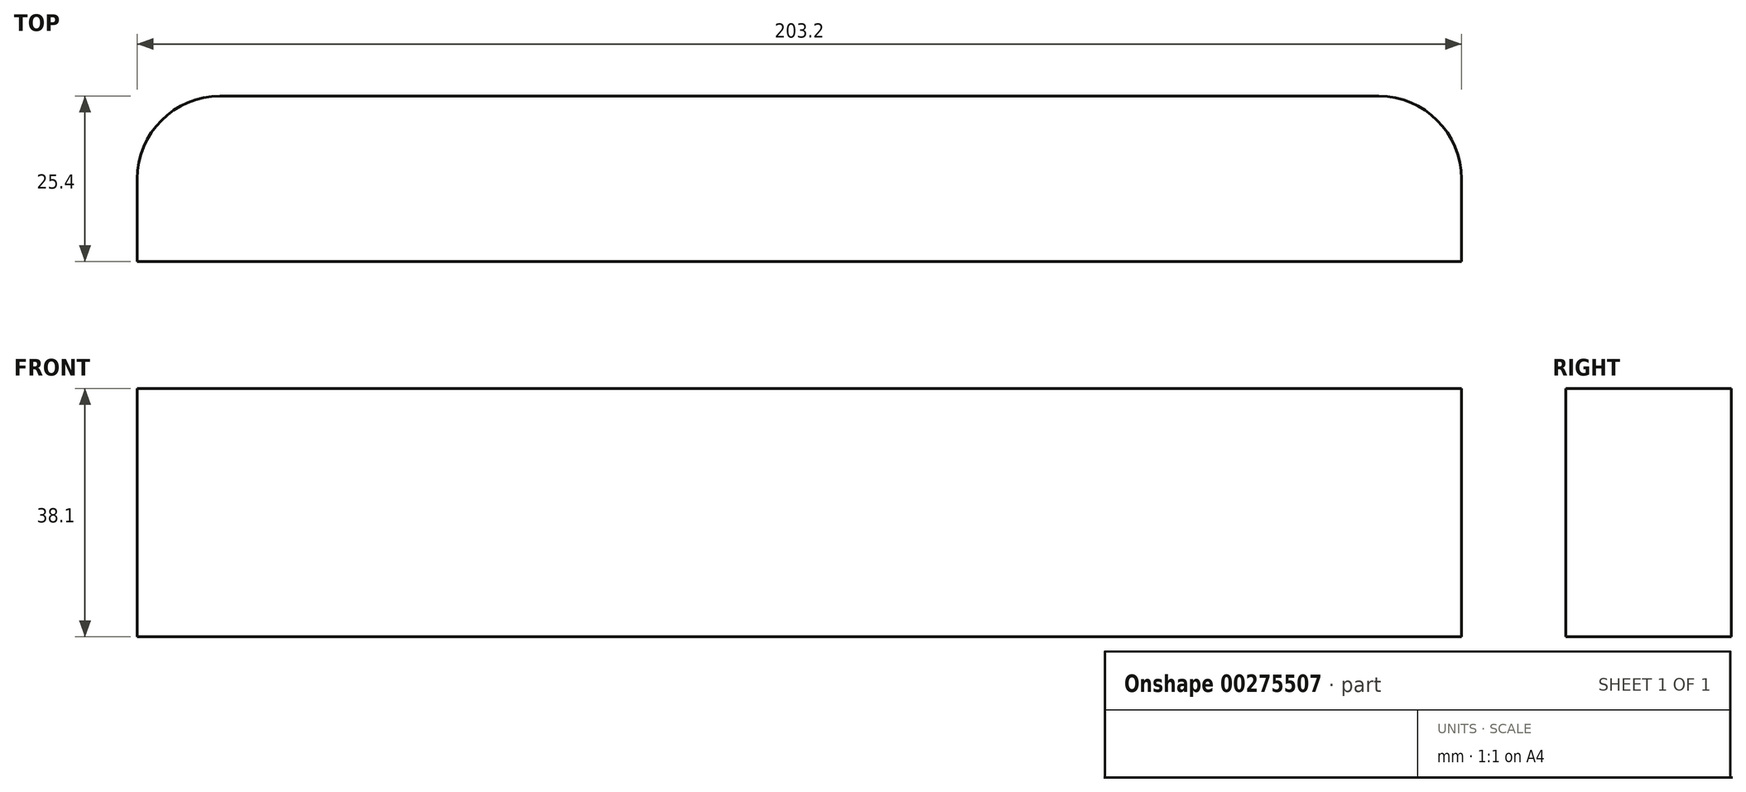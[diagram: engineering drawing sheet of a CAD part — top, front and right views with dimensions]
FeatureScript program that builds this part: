
annotation { "Feature Type Name" : "Feature", "Feature Type Description" : "" }
export const myFeature = defineFeature(function(context is Context, id is Id, definition is map)
    precondition{}
    {
        {
            var Q0;
            Q0=qCreatedBy(makeId("Top.planeOp"),FACE);
            var sketch = newSketch(context, id + "F0", { "sketchPlane" : qUnion([Q0])});
            skLineSegment(sketch, "E0.bottom", {"start": v(-80.27, 58.74) * mm, "end": v(97.53, 58.74) * mm});
            skLineSegment(sketch, "E0.top", {"start": v(-92.97, 33.34) * mm, "end": v(110.23, 33.34) * mm});
            skLineSegment(sketch, "E0.left", {"start": v(-92.97, 46.04) * mm, "end": v(-92.97, 33.34) * mm});
            skLineSegment(sketch, "E0.right", {"start": v(110.23, 46.04) * mm, "end": v(110.23, 33.34) * mm});
            skLineSegment(sketch, "E1.bottom", {"start": v(-92.97, 33.34) * mm, "end": v(-57.4, 33.34) * mm});
            skLineSegment(sketch, "E1.top", {"start": v(-92.97, -42.86) * mm, "end": v(-57.4, -42.86) * mm});
            skLineSegment(sketch, "E1.left", {"start": v(-92.97, 33.34) * mm, "end": v(-92.97, -42.86) * mm});
            skLineSegment(sketch, "E1.right", {"start": v(-57.4, 33.34) * mm, "end": v(-57.4, -42.86) * mm});
            skLineSegment(sketch, "E2.bottom", {"start": v(110.23, 33.34) * mm, "end": v(74.67, 33.34) * mm});
            skLineSegment(sketch, "E2.top", {"start": v(110.23, -42.86) * mm, "end": v(74.67, -42.86) * mm});
            skLineSegment(sketch, "E2.left", {"start": v(110.23, 33.34) * mm, "end": v(110.23, -42.86) * mm});
            skLineSegment(sketch, "E2.right", {"start": v(74.67, 33.34) * mm, "end": v(74.67, -42.86) * mm});
            skPoint(sketch, "E3.visualSharp", {"position": v(-92.97, 58.74) * mm});
            skArc(sketch, "E3.filletArc", {"start": v(-80.27, 58.74) * mm, "mid": v(-89.25, 55.02) * mm, "end": v(-92.97, 46.04) * mm});
            skPoint(sketch, "E4.visualSharp", {"position": v(110.23, 58.74) * mm});
            skArc(sketch, "E4.filletArc", {"start": v(110.23, 46.04) * mm, "mid": v(106.51, 55.02) * mm, "end": v(97.53, 58.74) * mm});
            skSolve(sketch);
        }
        {
            var Q0;
            Q0=makeQuery(id+"F0.imprint","IMPRINT",FACE,{"disambiguationData":[TD([[makeQuery(id+"F0.imprint","IMPRINT",EDGE,{"derivedFrom":sQuery(id+"F0.wireOp",EDGE,"E0.bottom")}),-1.0]])]});
            var Q1;
            Q1=makeQuery(id+"F0.imprint","IMPRINT",FACE,{"disambiguationData":[TD([[makeQuery(id+"F0.imprint","IMPRINT",EDGE,{"derivedFrom":sQuery(id+"F0.wireOp",EDGE,"E1.bottom")}),-1.0]])]});
            var Q2;
            Q2=makeQuery(id+"F0.imprint","IMPRINT",FACE,{"disambiguationData":[TD([[makeQuery(id+"F0.imprint","IMPRINT",EDGE,{"derivedFrom":sQuery(id+"F0.wireOp",EDGE,"E2.bottom")}),1.0]])]});
            extrude(context, id + "F1", {"entities" : qUnion([Q0, Q1, Q2]), "depth" : 38.1 * mm});
        }
    });
